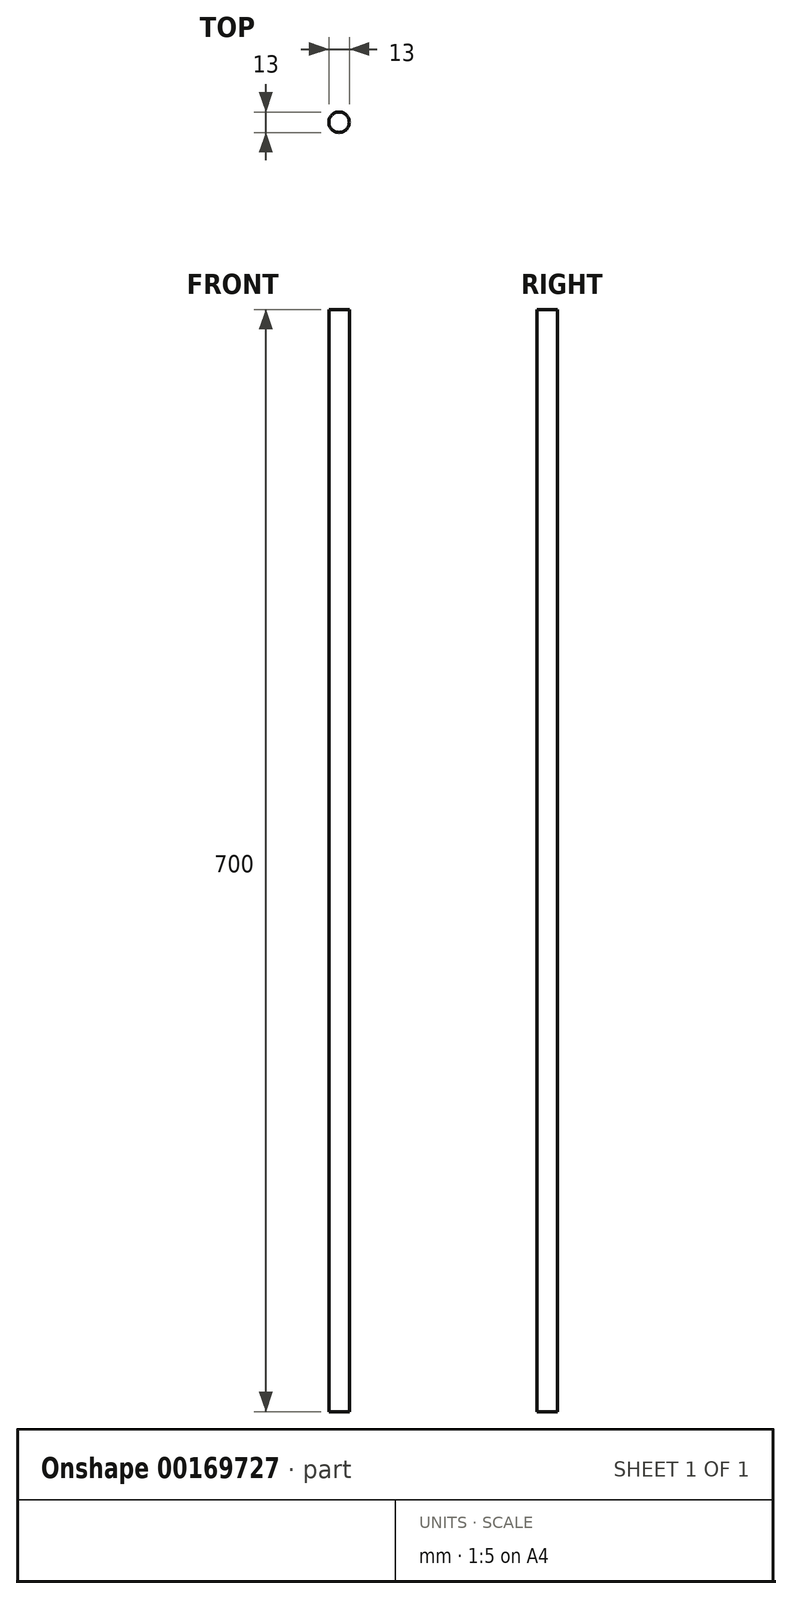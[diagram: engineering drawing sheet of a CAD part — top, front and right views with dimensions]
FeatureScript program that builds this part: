
annotation { "Feature Type Name" : "Feature", "Feature Type Description" : "" }
export const myFeature = defineFeature(function(context is Context, id is Id, definition is map)
    precondition{}
    {
        {
            var Q0;
            Q0=qCreatedBy(makeId("Top.planeOp"),FACE);
            var sketch = newSketch(context, id + "F0", { "sketchPlane" : qUnion([Q0])});
            skCircle(sketch, "E0", {"center": v(0, 0) * mm, "radius": 6.5 * mm});
            skSolve(sketch);
        }
        {
            var Q0;
            Q0=qSketchRegion(id+"F0",true);
            extrude(context, id + "F1", {"entities" : qUnion([Q0]), "endBound" : BoundingType.SYMMETRIC, "depth" : 700 * mm});
        }
    });
